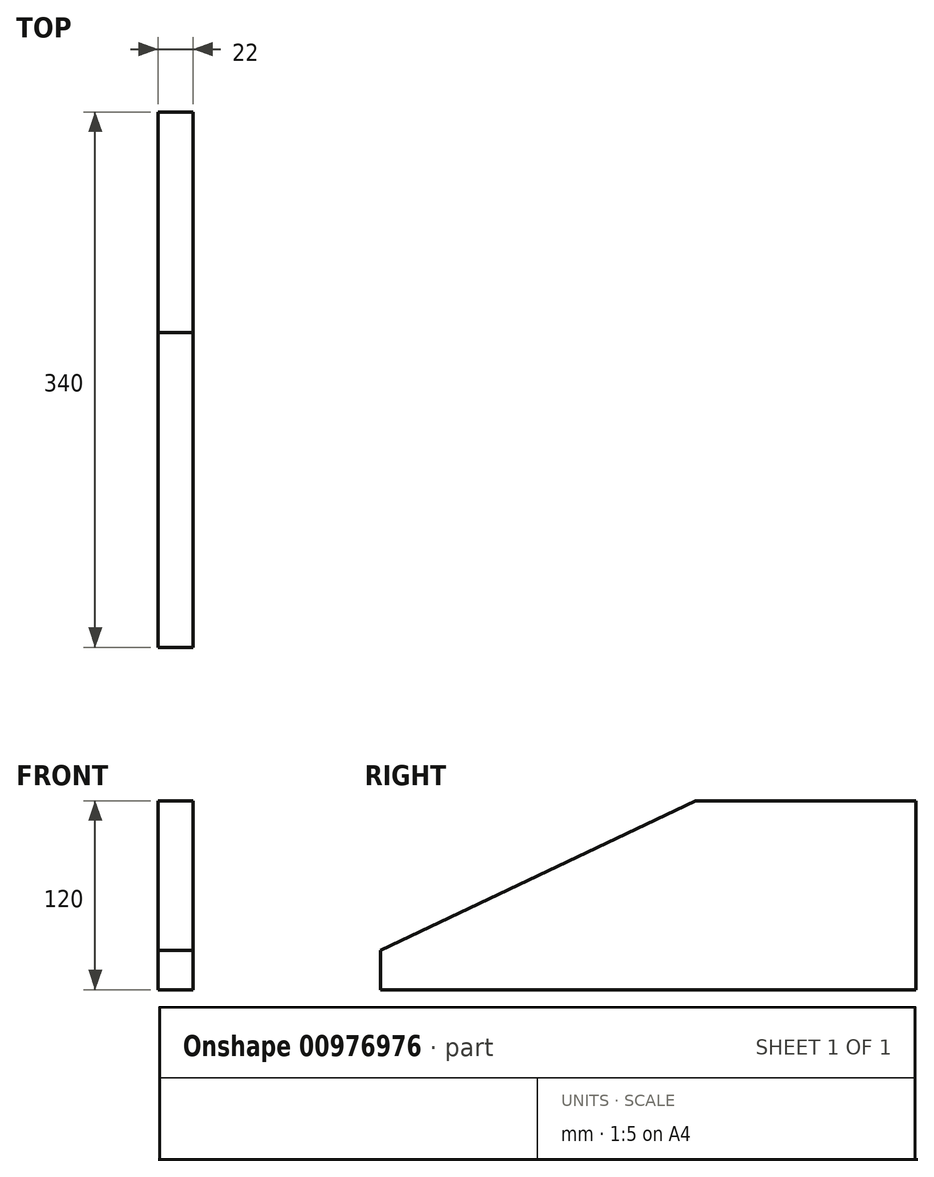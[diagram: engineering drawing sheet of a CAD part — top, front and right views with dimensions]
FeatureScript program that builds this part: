
annotation { "Feature Type Name" : "Feature", "Feature Type Description" : "" }
export const myFeature = defineFeature(function(context is Context, id is Id, definition is map)
    precondition{}
    {
        {
            var Q0;
            Q0=qCreatedBy(makeId("Right.planeOp"),FACE);
            var sketch = newSketch(context, id + "F0", { "sketchPlane" : qUnion([Q0])});
            skLineSegment(sketch, "E0", {"start": v(0, 0) * mm, "end": v(-340, 0) * mm});
            skLineSegment(sketch, "E1", {"start": v(0, 0) * mm, "end": v(0, 120) * mm});
            skLineSegment(sketch, "E2", {"start": v(0, 120) * mm, "end": v(-140, 120) * mm});
            skLineSegment(sketch, "E3", {"start": v(-140, 120) * mm, "end": v(-340, 25) * mm});
            skLineSegment(sketch, "E4", {"start": v(-340, 25) * mm, "end": v(-340, 0) * mm});
            skSolve(sketch);
        }
        {
            var Q0;
            Q0 = qSketchRegion(id + "F0", true);
            extrude(context, id + "F1", {"entities" : qUnion([Q0]), "depth" : 22 * mm, "offsetDistance" : 25 * mm});
        }
    });
